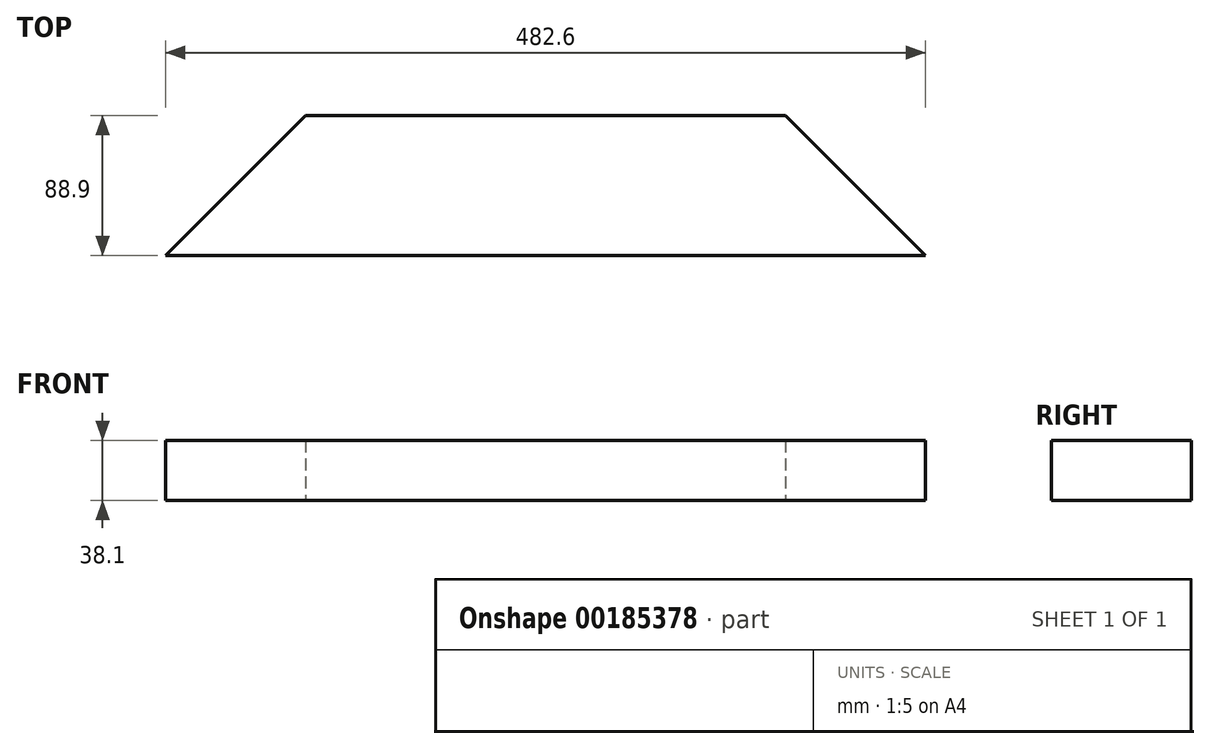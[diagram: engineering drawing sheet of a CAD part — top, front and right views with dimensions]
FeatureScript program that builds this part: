
annotation { "Feature Type Name" : "Feature", "Feature Type Description" : "" }
export const myFeature = defineFeature(function(context is Context, id is Id, definition is map)
    precondition{}
    {
        {
            var Q0;
            Q0=qCreatedBy(makeId("Top.planeOp"),FACE);
            var sketch = newSketch(context, id + "F0", { "sketchPlane" : qUnion([Q0])});
            skLineSegment(sketch, "E0", {"start": v(0, 0) * mm, "end": v(482.6, 0) * mm});
            skLineSegment(sketch, "E1", {"start": v(88.9, 88.9) * mm, "end": v(393.7, 88.9) * mm});
            skLineSegment(sketch, "E2", {"start": v(0, 0) * mm, "end": v(88.9, 88.9) * mm});
            skLineSegment(sketch, "E3", {"start": v(482.6, 0) * mm, "end": v(393.7, 88.9) * mm});
            skSolve(sketch);
        }
        {
            var Q0;
            Q0=makeQuery(id+"F0.imprint","IMPRINT",FACE,{"disambiguationData":[TD([[makeQuery(id+"F0.imprint","IMPRINT",EDGE,{"derivedFrom":sQuery(id+"F0.wireOp",EDGE,"E0")}),1.0]])]});
            extrude(context, id + "F1", {"entities" : qUnion([Q0]), "depth" : 38.1 * mm});
        }
    });
